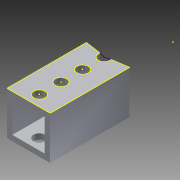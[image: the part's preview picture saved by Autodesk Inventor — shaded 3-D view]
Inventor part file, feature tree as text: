
AUTODESK INVENTOR PART (.ipt)
format: ipt  version: 2013 (Build 170138000, 138)  size: 163,840 bytes
history: native  units: in
note: dims shown in document units (in); Inventor stores cm internally (conversion verified against a paired STEP export)
features: extrude x5, sketch x5
ambient origin geometry x8: Origin, YZ Plane, XZ Plane, XY Plane, X Axis, Y Axis, Z Axis, Center Point
bodies: Solid1 (feature_tree)
feature tree (10):
  extrude  "Extrusion1"  Depth=1.0in
  extrude  "Extrusion2"  Depth=2.85in TaperAngle=0.0deg
  extrude  "Extrusion3"  Depth=0.075in
  extrude  "Extrusion4"  Depth=0.25in
  extrude  "Extrusion5"  Depth=1.9685in
  sketch  "Sketch6"  dims[d13=0.266in d14=1.9685in d16=0.5in d17=0.3937in d19=1.0in d21=1.0in d22=0.0in d23=1.0in d24=90.0deg d25=1.0in d26=90.0deg d27=1.0in d28=0.0in d29=1.0in d30=0.0in]
  sketch  "Sketch1"  dims[d2=1.0in d4=1.0in]
  sketch  "Sketch3"  dims[d5=0.125in d6=2.85in d7=0.0in]
  sketch  "Sketch4"  dims[d8=0.075in d9=0.075in]
  sketch  "Sketch5"  dims[d10=1.0in d11=0.0in d12=0.25in]
